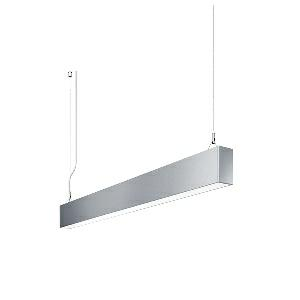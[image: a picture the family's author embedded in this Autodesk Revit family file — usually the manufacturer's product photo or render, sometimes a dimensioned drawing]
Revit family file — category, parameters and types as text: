
# Revit family: dotoo_line_-_dlp_1500_830_d_00805843_1b67
name_source: partatom
category: Lighting Fixtures
units: mm (PartAtom-declared; Revit-internal decimal feet)

## family parameters
Cut with Voids When Loaded = No
Host = Face
Light Source = No
Part Type = Normal
Room Calculation Point = No
Round Connector Dimension = Use Diameter
Shared = No

## types (1)
- DOTOO.line - DLP 1500/830/D (1 x LED, 1300 lm, 3000K)
    Apparent Load = 13 VA
    Approval mark = CE
    CIE Flux Codes = 67 91 98 100 100
    Color Rendering = 80-89
    Color Temperature = 3000K
    Control Gear = Electronic ballast
    Default Elevation = 1800 mm
    Description = DLP 1500/830/D|Suspended luminaire|light source: LED|connected load: 220-240 V, 50/60 Hz|Power consumption: approx. 13 W|standby: approx. 0,20|luminous flux: 1300 lm|luminous efficacy: 100 lm/W|light distribution: Direct|direct ratio: approx. 100 %|colour temperature: Warm white, ca. 3000 K|color rendering index (CRI): >= 80|chromaticity tolerance:  3 SDCM|System of protection: IP 40|technology: Continuously dimmable|luminaire body|material: Sectional aluminium|colour: Silver|lamp cover: Acrylic (PMMA), Clear|mains lead: 2.00 m With free stranded wires|Fastening: Steel cable 0.3 - 0.7 m|glare control: Prism aperture|luminance(L65): <= 3000 cd/m|unified glare rating(4H 8H): <=  19|special features: DALI Load 1x, TouchDIM - dimming via standard switch, Flicker-free, Suitable as emergency lighting|
    Frequency = 50 Hz
    Height = 110 mm
    Lamp = 1 x LED
    Lamp Light Flux = 1300 lm
    Lamp count = 1
    Length = 1134 mm
    Luminous efficacy = 100 lm/W
    Manufacturer = Waldmann
    ModVariant = No
    Model = 00805843
    Mounting Place = Ceiling
    Mounting Type = Pendant
    Number of Poles = 1
    OnlyDefault = Yes
    Power Factor = 1
    Product Name = DOTOO.line - DLP 1500/830/D
    Product group = Suspended luminaire
    ProductGroupID = 9
    Protection Class = Protection class I
    Protection Degree = IP 40
    RLX_Detail_Level = 1
    RLX_Emergency_Light_Flux = 0 lm
    RLX_Emergency_Type = 0
    RLX_Emergency_Type_DB = No
    RlxData = <blob elided: 21045 chars, md5=d84ae63b>
    Socket = socket
    Standby Power = 0 W
    System Light Flux = 1300 lm
    System Power = 13 W
    Type Comments = Product without accessories
    Type Image = 113290000-00692519.jpg
    URL = http://relux.com
    VarID = ---
    Voltage = 230 V
    Voltage Range = 220-240 V
    Weight = 0.00 kg
    Width = 60 mm  [stored 0.19685 ft]

note: [stored X ft] marks values corroborated as IEEE doubles in the binary element streams (Revit-internal decimal feet)

## geometry (parser evidence)
native form markers: Blend x4, Sweep x11
no freeform markers — native parametric forms only
